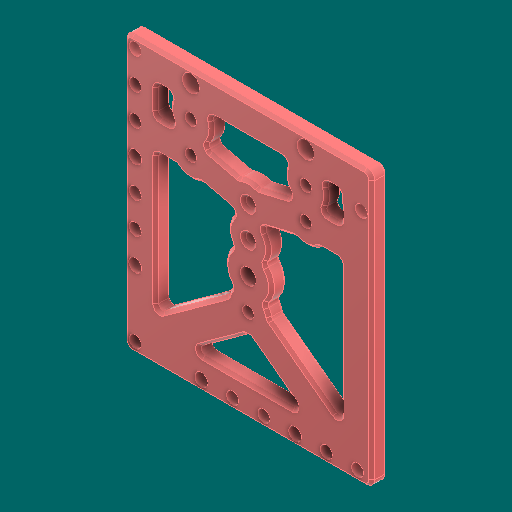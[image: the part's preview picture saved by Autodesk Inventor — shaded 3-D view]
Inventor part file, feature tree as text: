
AUTODESK INVENTOR PART (.ipt)
format: ipt  version: 2023.1 (Build 271208000, 208)  size: 1,120,768 bytes
history: native  units: in
note: dims shown in document units (in); Inventor stores cm internally (conversion verified against a paired STEP export)
features: reference x4, other x4, extrude x2, chamfer x2, sketch x2, fillet x1, projected_geometry x1
ambient origin geometry x8: Origin, YZ Plane, XZ Plane, XY Plane, X Axis, Y Axis, Z Axis, Center Point
bodies: Solid1 (feature_tree)
feature tree (16):
  extrude  "Extrusion1"  Depth=0.18in
  extrude  "Extrusion2"  Depth=0.0625in
  fillet  "Fillet2"  Radius=0.5in
  chamfer  "Chamfer1"  Distance=0.18in
  chamfer  "Chamfer2"  Distance=0.5in
  sketch  "Sketch1"  dims[d0=0.5in d1=0.18in]
  reference  "Reference1"
  reference  "Reference2"
  reference  "Reference3"
  reference  "Reference4"
  sketch  "Sketch2"  dims[d2=0.5in d3=0.18in d4=0.5in d5=0.18in d6=0.5in d7=0.18in d8=0.25in d9=0.5in d10=0.1562in d11=0.5in d12=0.5in d13=0.18in d14=0.25in d15=0.0in d16=0.5in d17=0.25in d18=0.25in d19=0.25in d20=0.25in d21=0.25in d22=0.25in d23=0.25in d24=0.25in d25=0.25in d26=0.25in d27=0.25in d28=0.25in d29=0.5in d30=0.5in d31=0.5in d32=0.5in d34=0.5in d35=0.5in d36=0.0in d37=0.0in d39=0.0625in d40=0.0472in d41=0.125in d42=45.0deg d43=0.0472in d44=0.125in d45=45.0deg]
  projected_geometry  "Projected Loop1"
  other  "<userpath>\Documents\CAD\guardSwerve5\MainAssy.iam"
  other  "MainAssy.iam"
  other  "Baseplate:1"
  other  "DiffCap:1"
